# Revit family: Hager-Univers-IP43-D349-H1048-Cl.II-Fire_res.encl_30min-NoHosted-PL-en
name_source: partatom
category: Equipement électrique
units: mm (PartAtom-declared; Revit-internal decimal feet)

## family parameters
Basée sur le plan de construction = Oui
Configuration du panneau = Deux colonnes, circuits au sein
Cote de connecteur circulaire = Utiliser le diamètre
Couper avec des vides une fois chargée = Non
Partagée = Non
Point de calcul de pièce = Non
Toujours verticalement = Oui
Type d'élément = Tableau de raccordement

## types (3) — shared parameters
Commentaires du type = Univers
EF000003 - Mounting method = EV000384 - Surface mounted (plaster)
EF000007 - Colour = EV000270 - Grey
EF000040 - Height = 1048 mm  [stored 3.43832 ft]
EF000049 - Depth = 349 mm  [stored 1.14501 ft]
EF000116 - RAL-number = 7035
EF000118 - With mounting plate = Non
EF000266 - Number of rows = 6
EF000339 - Type of cover = EV004216 - Door
EF001088 - Extension possible = Non
EF001131 - Internal depth = 240 mm  [stored 0.787402 ft]
EF001596 - Material housing = EV000139 - Plastic
EF001613 - Circuit integrity = EV004178 - E30
EF003532 - Suitable for outdoor use = Non
EF004293 - Impact strength = EV008784 - IK10
EF004464 - Type of door = EV002646 - Single
EF005474 - Degree of protection (IP) = EV006610 - IP43
EF006244 - Transparent cover/door = Non
EF006306 - With lock = Oui
EF007800 - Suitable for lightning protection = Non
EF008873 - Nominal current (In) = 250 A
EF009170 - Material plate thickness cabinet = 70 mm  [stored 0.229659 ft]
EF009171 - Material plate thickness door/cover = 22 mm  [stored 0.0721785 ft]
EF009212 - Cover model = EV000116 - Closed
EF015940 - Cover with overpressure release = Non
Elévation par défaut = 1219 mm
Fabricant = Hager
HG000002 - With door or cover = Oui
HG000003 - Range = Univers
HG000006 - Flush mounted = Non
HG000009 - Double swing door = Non
HG000010 - Asymmetric doors = Non
HG000023 - Double section enclosure = Non
HG000024 - Bottom section height = 600 mm
HG000026 - Floor standing = Non
zero-valued in all types: EF000218 - Built-in depth, HG000027 - Plinth height

## per-type parameters (varying)
| type | EF000008 - Width | EF000437 - Number of conduit inlets | EF002950 - Width in number of modular spacings | EF004427 - Number of modules | EF009554 - Number of openings for flange plates | HG000004 - Manufacturer reference |
| Surface mounted (plaster) IP43 W398 H1048 D349  - FB61LE | 398 mm  [stored 1.30577 ft] | 1 | 12 | 72 | 2 | FB61LE |
| Surface mounted (plaster) IP43 W648 H1048 D349  - FB62LE | 648 mm  [stored 2.12598 ft] | 2 | 24 | 144 | 4 | FB62LE |
| Surface mounted (plaster) IP43 W898 H1048 D349  - FB63LE | 898 mm  [stored 2.94619 ft] | 3 | 36 | 216 | 6 | FB63LE |

note: [stored X ft] marks values corroborated as IEEE doubles in the binary element streams (Revit-internal decimal feet)

## geometry (parser evidence)
native form markers: Blend x4, Sweep x5
no freeform markers — native parametric forms only
